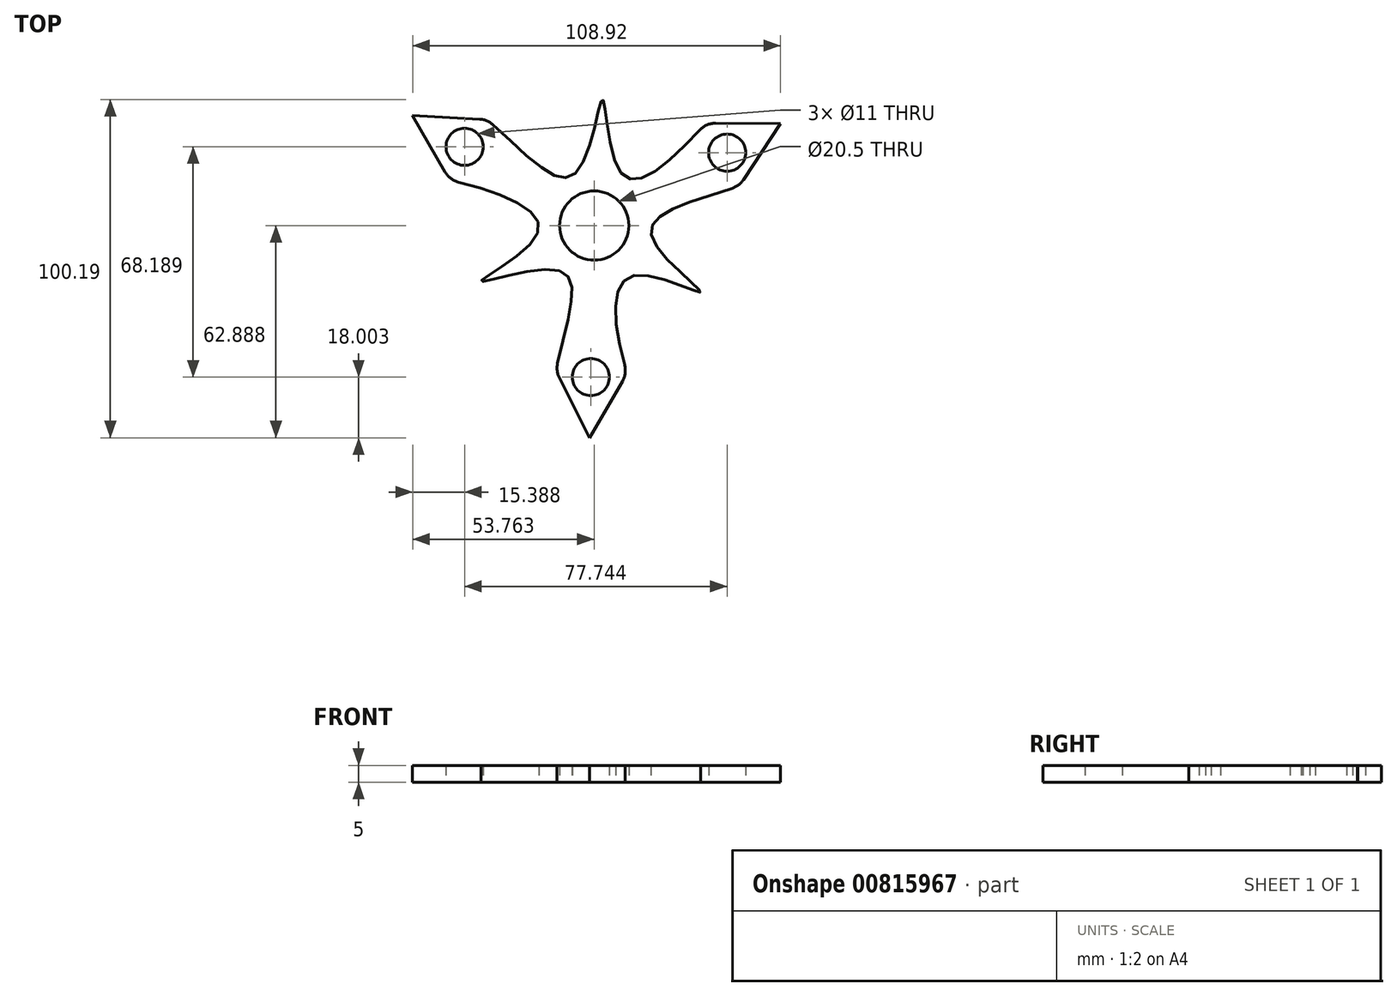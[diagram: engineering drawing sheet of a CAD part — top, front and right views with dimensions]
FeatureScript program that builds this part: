
annotation { "Feature Type Name" : "Feature", "Feature Type Description" : "" }
export const myFeature = defineFeature(function(context is Context, id is Id, definition is map)
    precondition{}
    {
        {
            var Q0;
            Q0=qCreatedBy(makeId("Top.planeOp"),FACE);
            var sketch = newSketch(context, id + "F0", { "sketchPlane" : qUnion([Q0])});
            skFitSpline(sketch, "E0", {"points": [v(-122.08, 62.93) * mm, v(-95.97, 47.46) * mm, v(-112.82, 32.98) * mm, v(-89.6, 36.06) * mm, v(-90.66, 6.4) * mm], "startDerivative": vector(148.23, -33.56) * mm, "endDerivative": vector(-34.89, -172.18) * mm});
            skFitSpline(sketch, "E1", {"points": [v(-69.6, 5.75) * mm, v(-67.72, 34.6) * mm, v(-47.88, 29.82) * mm, v(-62.28, 46.13) * mm, v(-36.36, 61.23) * mm], "startDerivative": vector(-45.07, 145.15) * mm, "endDerivative": vector(166.52, 56) * mm});
            skFitSpline(sketch, "E2", {"points": [v(-46.22, 79.77) * mm, v(-70.96, 64.5) * mm, v(-76.86, 86.8) * mm, v(-84.66, 65.11) * mm, v(-111, 80.84) * mm], "startDerivative": vector(-103.18, -111.6) * mm, "endDerivative": vector(-131.66, 116.31) * mm});
            skLineSegment(sketch, "E3", {"start": v(-123.45, 65.32) * mm, "end": v(-133.1, 82.14) * mm});
            skLineSegment(sketch, "E4", {"start": v(-133.1, 82.14) * mm, "end": v(-113.2, 80.97) * mm});
            skPoint(sketch, "E5.center", {"position": v(-79.34, 49.49) * mm});
            skLineSegment(sketch, "E6.1.0", {"start": v(-80.73, -13.4) * mm, "end": v(-89.66, 4.41) * mm});
            skLineSegment(sketch, "E6.1.1", {"start": v(-70.98, 3.38) * mm, "end": v(-80.73, -13.4) * mm});
            skLineSegment(sketch, "E6.2.0", {"start": v(-24.18, 79.73) * mm, "end": v(-35.15, 63.07) * mm});
            skLineSegment(sketch, "E6.2.1", {"start": v(-43.43, 79.78) * mm, "end": v(-24.18, 79.73) * mm});
            skArc(sketch, "E7.filletArc", {"start": v(-109.32, 79.34) * mm, "mid": v(-111.12, 80.49) * mm, "end": v(-113.2, 80.97) * mm});
            skArc(sketch, "E8.filletArc", {"start": v(-123.45, 65.32) * mm, "mid": v(-121.77, 63.4) * mm, "end": v(-119.46, 62.3) * mm});
            skArc(sketch, "E9.filletArc", {"start": v(-90.2, 8.62) * mm, "mid": v(-90.29, 6.47) * mm, "end": v(-89.66, 4.41) * mm});
            skArc(sketch, "E10.filletArc", {"start": v(-70.98, 3.38) * mm, "mid": v(-70.17, 5.78) * mm, "end": v(-70.36, 8.3) * mm});
            skArc(sketch, "E11.filletArc", {"start": v(-38.47, 60.53) * mm, "mid": v(-36.6, 61.52) * mm, "end": v(-35.15, 63.07) * mm});
            skPoint(sketch, "E12.newPointB", {"position": v(-46.32, 79.79) * mm});
            skArc(sketch, "E12.filletArc", {"start": v(-43.43, 79.78) * mm, "mid": v(-45.96, 79.26) * mm, "end": v(-48.08, 77.77) * mm});
            skCircle(sketch, "E13", {"center": v(-79.34, 49.49) * mm, "radius": 10.25 * mm});
            skPoint(sketch, "E14.visualSharp", {"position": v(-73.9, 8.33) * mm});
            skPoint(sketch, "E15.visualSharp", {"position": v(-86.6, 8.62) * mm});
            skPoint(sketch, "E16.visualSharp", {"position": v(-80.49, -2.52) * mm});
            skPoint(sketch, "E17.visualSharp", {"position": v(-117.7, 65.35) * mm});
            skPoint(sketch, "E18.visualSharp", {"position": v(-123.8, 76.49) * mm});
            skPoint(sketch, "E19.visualSharp", {"position": v(-111.1, 76.2) * mm});
            skPoint(sketch, "E20.visualSharp", {"position": v(-40.31, 63.64) * mm});
            skPoint(sketch, "E21.visualSharp", {"position": v(-33.72, 74.5) * mm});
            skPoint(sketch, "E22.visualSharp", {"position": v(-46.42, 74.78) * mm});
            skCircle(sketch, "E23", {"center": v(-117.71, 72.8) * mm, "radius": 5.5 * mm});
            skLineSegment(sketch, "E24", {"start": v(-133.1, 82.14) * mm, "end": v(-79.34, 49.49) * mm});
            skCircle(sketch, "E25.1.0", {"center": v(-80.33, 4.6) * mm, "radius": 5.5 * mm});
            skCircle(sketch, "E25.2.0", {"center": v(-39.97, 71.07) * mm, "radius": 5.5 * mm});
            skSolve(sketch);
        }
        {
            var Q0;
            Q0=makeQuery(id+"F0.imprint","IMPRINT",FACE,{"disambiguationData":[TD([[makeQuery(id+"F0.imprint","IMPRINT",EDGE,{"derivedFrom":sQuery(id+"F0.wireOp",EDGE,"E0")}),1.0]])]});
            extrude(context, id + "F1", {"entities" : qUnion([Q0]), "depth" : 5 * mm, "offsetDistance" : 25.4 * mm});
        }
    });
